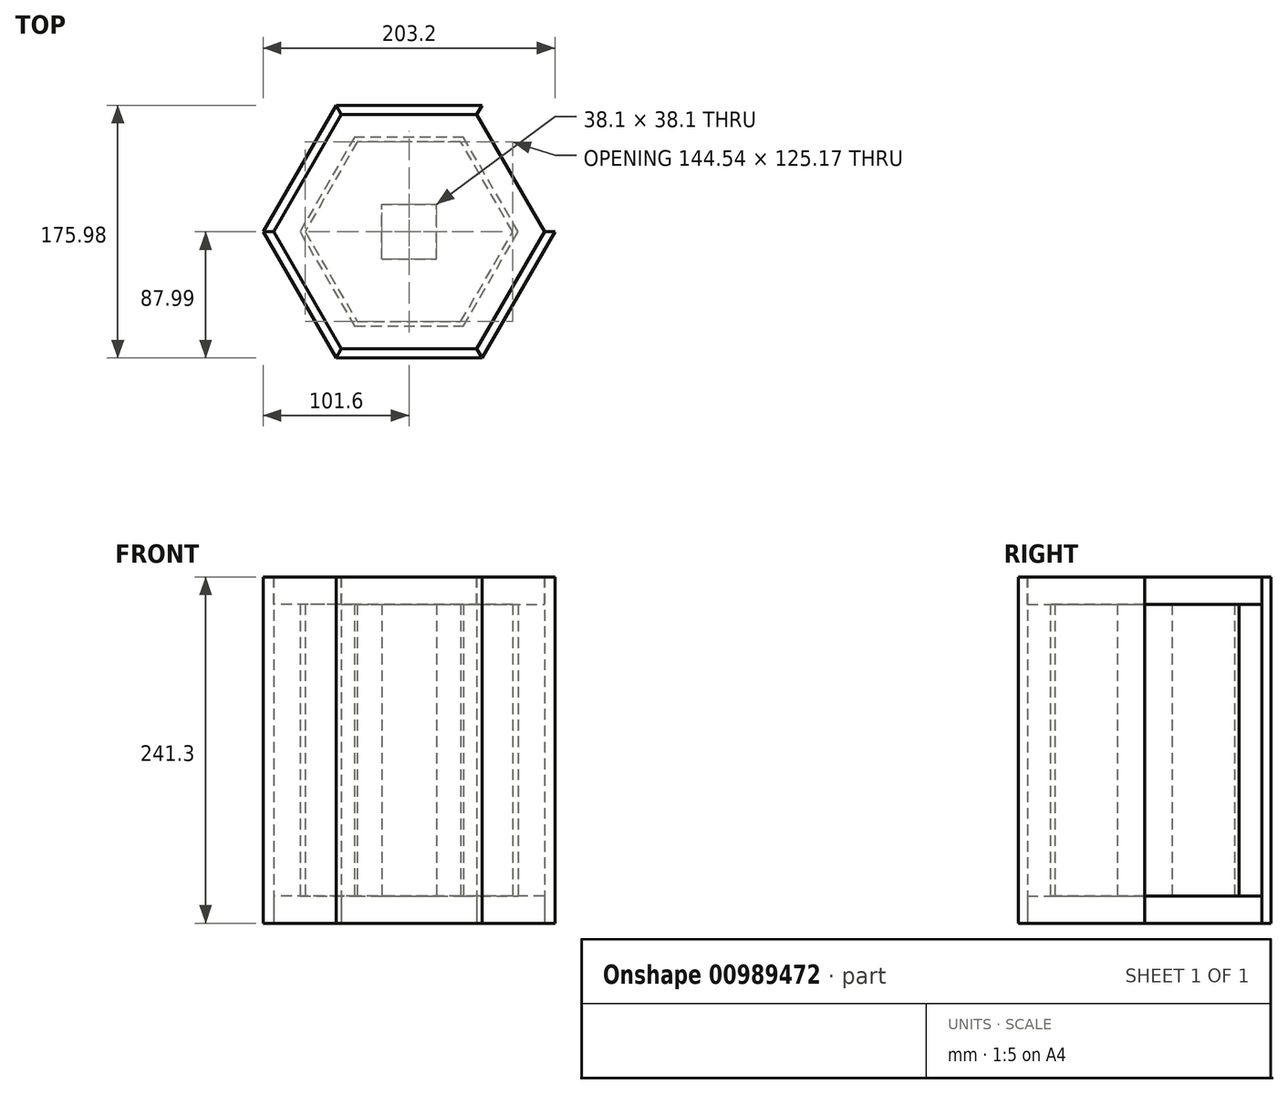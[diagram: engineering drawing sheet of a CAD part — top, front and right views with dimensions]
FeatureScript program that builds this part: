
annotation { "Feature Type Name" : "Feature", "Feature Type Description" : "" }
export const myFeature = defineFeature(function(context is Context, id is Id, definition is map)
    precondition{}
    {
        {
            var Q0;
            Q0=qCreatedBy(makeId("Top.planeOp"),FACE);
            var sketch = newSketch(context, id + "F0", { "sketchPlane" : qUnion([Q0])});
            skCircle(sketch, "E0.cCircle", {"center": v(0, 0) * mm, "radius": 87.99 * mm, "construction": true});
            skLineSegment(sketch, "E0.0", {"start": v(50.8, -87.99) * mm, "end": v(-50.8, -87.99) * mm});
            skLineSegment(sketch, "E0.1", {"start": v(-50.8, -87.99) * mm, "end": v(-101.6, 0) * mm});
            skLineSegment(sketch, "E0.2", {"start": v(-101.6, 0) * mm, "end": v(-50.8, 87.99) * mm});
            skLineSegment(sketch, "E0.3", {"start": v(-50.8, 87.99) * mm, "end": v(50.8, 87.99) * mm});
            skLineSegment(sketch, "E0.4", {"start": v(50.8, 87.99) * mm, "end": v(101.6, 0) * mm});
            skLineSegment(sketch, "E0.5", {"start": v(101.6, 0) * mm, "end": v(50.8, -87.99) * mm});
            skPoint(sketch, "E0.0.midPoint", {"position": v(0, -87.99) * mm});
            skLineSegment(sketch, "E1.0", {"start": v(-47.13, -81.64) * mm, "end": v(-94.26, 0) * mm});
            skLineSegment(sketch, "E1.1", {"start": v(-47.13, 81.64) * mm, "end": v(47.13, 81.64) * mm});
            skLineSegment(sketch, "E1.2", {"start": v(47.13, 81.64) * mm, "end": v(94.26, 0) * mm});
            skLineSegment(sketch, "E1.3", {"start": v(-94.26, 0) * mm, "end": v(-47.13, 81.64) * mm});
            skLineSegment(sketch, "E1.4", {"start": v(94.26, 0) * mm, "end": v(47.13, -81.64) * mm});
            skLineSegment(sketch, "E1.5", {"start": v(47.13, -81.64) * mm, "end": v(-47.13, -81.64) * mm});
            skLineSegment(sketch, "E2", {"start": v(-50.8, 87.99) * mm, "end": v(-47.13, 81.64) * mm});
            skLineSegment(sketch, "E3", {"start": v(47.13, 81.64) * mm, "end": v(50.8, 87.99) * mm});
            skLineSegment(sketch, "E4", {"start": v(101.6, 0) * mm, "end": v(94.26, 0) * mm});
            skLineSegment(sketch, "E5", {"start": v(47.13, -81.64) * mm, "end": v(50.8, -87.99) * mm});
            skLineSegment(sketch, "E6", {"start": v(-50.8, -87.99) * mm, "end": v(-47.13, -81.64) * mm});
            skLineSegment(sketch, "E7", {"start": v(-101.6, 0) * mm, "end": v(-94.26, 0) * mm});
            skSolve(sketch);
        }
        {
            var Q0;
            Q0=makeQuery(id+"F0.imprint","IMPRINT",FACE,{"disambiguationData":[TD([[makeQuery(id+"F0.imprint","IMPRINT",EDGE,{"derivedFrom":sQuery(id+"F0.wireOp",EDGE,"E1.0")}),-1.0]])]});
            extrude(context, id + "F1", {"entities" : qUnion([Q0]), "depth" : 19.05 * mm, "offsetDistance" : 25.4 * mm});
        }
        {
            var Q0;
            Q0=makeQuery(id+"F1.opExtrude","CAP_FACE",FACE,{"disambiguationData":[OSD([sQuery(id+"F0.wireOp",EDGE,"E1.0"),sQuery(id+"F0.wireOp",EDGE,"E1.1"),sQuery(id+"F0.wireOp",EDGE,"E1.2"),sQuery(id+"F0.wireOp",EDGE,"E1.3"),sQuery(id+"F0.wireOp",EDGE,"E1.4"),sQuery(id+"F0.wireOp",EDGE,"E1.5")])],"isStart":false});
            var sketch = newSketch(context, id + "F2", { "sketchPlane" : qUnion([Q0])});
            skLineSegment(sketch, "E8.bottom", {"start": v(-19.05, -19.05) * mm, "end": v(19.05, -19.05) * mm});
            skLineSegment(sketch, "E8.top", {"start": v(-19.05, 19.05) * mm, "end": v(19.05, 19.05) * mm});
            skLineSegment(sketch, "E8.left", {"start": v(-19.05, -19.05) * mm, "end": v(-19.05, 19.05) * mm});
            skLineSegment(sketch, "E8.right", {"start": v(19.05, -19.05) * mm, "end": v(19.05, 19.05) * mm});
            skSolve(sketch);
        }
        {
            var Q0;
            Q0=makeQuery(id+"F2.imprint","IMPRINT",FACE,{"disambiguationData":[TD([[makeQuery(id+"F2.imprint","IMPRINT",EDGE,{"derivedFrom":sQuery(id+"F2.wireOp",EDGE,"E8.bottom")}),1.0]])]});
            extrude(context, id + "F3", {"entities" : qUnion([Q0]), "depth" : 203.2 * mm, "offsetDistance" : 25.4 * mm});
        }
        {
            var Q0;
            Q0=makeQuery(id+"F1.opExtrude","CAP_FACE",FACE,{"disambiguationData":[OSD([sQuery(id+"F0.wireOp",EDGE,"E1.0"),sQuery(id+"F0.wireOp",EDGE,"E1.1"),sQuery(id+"F0.wireOp",EDGE,"E1.2"),sQuery(id+"F0.wireOp",EDGE,"E1.3"),sQuery(id+"F0.wireOp",EDGE,"E1.4"),sQuery(id+"F0.wireOp",EDGE,"E1.5")])],"isStart":false});
            cPlane(context, id + "F4", {"entities" : qUnion([Q0]), "cplaneType" : CPlaneType.OFFSET, "offset" : 101.6 * mm, "width" : 152.4 * mm, "height" : 152.4 * mm});
        }
        {
            var Q0;
            Q0=makeQuery(id+"F1.opExtrude","SWEPT_BODY",BODY,{"disambiguationData":[OSD([sQuery(id+"F0.wireOp",EDGE,"E1.0"),sQuery(id+"F0.wireOp",EDGE,"E1.1"),sQuery(id+"F0.wireOp",EDGE,"E1.2"),sQuery(id+"F0.wireOp",EDGE,"E1.3"),sQuery(id+"F0.wireOp",EDGE,"E1.4"),sQuery(id+"F0.wireOp",EDGE,"E1.5")])]});
            var Q1;
            Q1=qCreatedBy(id+"F4.planeOp",FACE);
            mirror(context, id + "F5", {"operationType" : NewBodyOperationType.ADD, "entities" : qUnion([Q0]), "mirrorPlane" : qUnion([Q1])});
        }
        {
            var Q0;
            Q0=makeQuery(id+"F0.imprint","IMPRINT",FACE,{"disambiguationData":[TD([[makeQuery(id+"F0.imprint","IMPRINT",EDGE,{"derivedFrom":sQuery(id+"F0.wireOp",EDGE,"E0.3")}),-1.0]])]});
            var Q1;
            Q1=makeQuery(id+"F5.opPattern","COPY",FACE,{"derivedFrom":makeQuery(id+"F1.opExtrude","CAP_FACE",FACE,{"disambiguationData":[OSD([sQuery(id+"F0.wireOp",EDGE,"E1.0"),sQuery(id+"F0.wireOp",EDGE,"E1.1"),sQuery(id+"F0.wireOp",EDGE,"E1.2"),sQuery(id+"F0.wireOp",EDGE,"E1.3"),sQuery(id+"F0.wireOp",EDGE,"E1.4"),sQuery(id+"F0.wireOp",EDGE,"E1.5")])],"isStart":true}),"instanceName":"1"});
            extrude(context, id + "F6", {"entities" : qUnion([Q0]), "endBound" : BoundingType.UP_TO_SURFACE, "depth" : 222.25 * mm, "endBoundEntityFace" : qUnion([Q1]), "offsetDistance" : 25.4 * mm});
        }
        {
            var Q0;
            Q0=makeQuery(id+"F0.imprint","IMPRINT",FACE,{"disambiguationData":[TD([[makeQuery(id+"F0.imprint","IMPRINT",EDGE,{"derivedFrom":sQuery(id+"F0.wireOp",EDGE,"E0.2")}),-1.0]])]});
            var Q1;
            Q1=makeQuery(id+"F5.opPattern","COPY",FACE,{"derivedFrom":makeQuery(id+"F1.opExtrude","CAP_FACE",FACE,{"disambiguationData":[OSD([sQuery(id+"F0.wireOp",EDGE,"E1.0"),sQuery(id+"F0.wireOp",EDGE,"E1.1"),sQuery(id+"F0.wireOp",EDGE,"E1.2"),sQuery(id+"F0.wireOp",EDGE,"E1.3"),sQuery(id+"F0.wireOp",EDGE,"E1.4"),sQuery(id+"F0.wireOp",EDGE,"E1.5")])],"isStart":true}),"instanceName":"1"});
            extrude(context, id + "F7", {"entities" : qUnion([Q0]), "endBound" : BoundingType.UP_TO_SURFACE, "depth" : 25.4 * mm, "endBoundEntityFace" : qUnion([Q1]), "offsetDistance" : 25.4 * mm});
        }
        {
            var Q0;
            Q0=makeQuery(id+"F0.imprint","IMPRINT",FACE,{"disambiguationData":[TD([[makeQuery(id+"F0.imprint","IMPRINT",EDGE,{"derivedFrom":sQuery(id+"F0.wireOp",EDGE,"E0.1")}),-1.0]])]});
            var Q1;
            Q1=makeQuery(id+"F5.opPattern","COPY",FACE,{"derivedFrom":makeQuery(id+"F1.opExtrude","CAP_FACE",FACE,{"disambiguationData":[OSD([sQuery(id+"F0.wireOp",EDGE,"E1.0"),sQuery(id+"F0.wireOp",EDGE,"E1.1"),sQuery(id+"F0.wireOp",EDGE,"E1.2"),sQuery(id+"F0.wireOp",EDGE,"E1.3"),sQuery(id+"F0.wireOp",EDGE,"E1.4"),sQuery(id+"F0.wireOp",EDGE,"E1.5")])],"isStart":true}),"instanceName":"1"});
            extrude(context, id + "F8", {"entities" : qUnion([Q0]), "endBound" : BoundingType.UP_TO_SURFACE, "depth" : 25.4 * mm, "endBoundEntityFace" : qUnion([Q1]), "offsetDistance" : 25.4 * mm});
        }
        {
            var Q0;
            Q0=makeQuery(id+"F0.imprint","IMPRINT",FACE,{"disambiguationData":[TD([[makeQuery(id+"F0.imprint","IMPRINT",EDGE,{"derivedFrom":sQuery(id+"F0.wireOp",EDGE,"E0.0")}),-1.0]])]});
            var Q1;
            Q1=makeQuery(id+"F5.opPattern","COPY",FACE,{"derivedFrom":makeQuery(id+"F1.opExtrude","CAP_FACE",FACE,{"disambiguationData":[OSD([sQuery(id+"F0.wireOp",EDGE,"E1.0"),sQuery(id+"F0.wireOp",EDGE,"E1.1"),sQuery(id+"F0.wireOp",EDGE,"E1.2"),sQuery(id+"F0.wireOp",EDGE,"E1.3"),sQuery(id+"F0.wireOp",EDGE,"E1.4"),sQuery(id+"F0.wireOp",EDGE,"E1.5")])],"isStart":true}),"instanceName":"1"});
            extrude(context, id + "F9", {"entities" : qUnion([Q0]), "endBound" : BoundingType.UP_TO_SURFACE, "depth" : 25.4 * mm, "endBoundEntityFace" : qUnion([Q1]), "offsetDistance" : 25.4 * mm});
        }
        {
            var Q0;
            Q0=makeQuery(id+"F0.imprint","IMPRINT",FACE,{"disambiguationData":[TD([[makeQuery(id+"F0.imprint","IMPRINT",EDGE,{"derivedFrom":sQuery(id+"F0.wireOp",EDGE,"E0.5")}),-1.0]])]});
            var Q1;
            Q1=makeQuery(id+"F5.opPattern","COPY",FACE,{"derivedFrom":makeQuery(id+"F1.opExtrude","CAP_FACE",FACE,{"disambiguationData":[OSD([sQuery(id+"F0.wireOp",EDGE,"E1.0"),sQuery(id+"F0.wireOp",EDGE,"E1.1"),sQuery(id+"F0.wireOp",EDGE,"E1.2"),sQuery(id+"F0.wireOp",EDGE,"E1.3"),sQuery(id+"F0.wireOp",EDGE,"E1.4"),sQuery(id+"F0.wireOp",EDGE,"E1.5")])],"isStart":true}),"instanceName":"1"});
            extrude(context, id + "F10", {"entities" : qUnion([Q0]), "endBound" : BoundingType.UP_TO_SURFACE, "depth" : 25.4 * mm, "endBoundEntityFace" : qUnion([Q1]), "offsetDistance" : 25.4 * mm});
        }
        {
            var Q0;
            Q0=makeQuery(id+"F1.opExtrude","CAP_FACE",FACE,{"disambiguationData":[OSD([sQuery(id+"F0.wireOp",EDGE,"E1.0"),sQuery(id+"F0.wireOp",EDGE,"E1.1"),sQuery(id+"F0.wireOp",EDGE,"E1.2"),sQuery(id+"F0.wireOp",EDGE,"E1.3"),sQuery(id+"F0.wireOp",EDGE,"E1.4"),sQuery(id+"F0.wireOp",EDGE,"E1.5")])],"isStart":false});
            var sketch = newSketch(context, id + "F11", { "sketchPlane" : qUnion([Q0])});
            skLineSegment(sketch, "E9.0", {"start": v(-36.13, -62.59) * mm, "end": v(-72.27, 0) * mm});
            skLineSegment(sketch, "E9.1", {"start": v(-36.13, 62.59) * mm, "end": v(36.13, 62.59) * mm});
            skLineSegment(sketch, "E9.2", {"start": v(36.13, 62.59) * mm, "end": v(72.27, 0) * mm});
            skLineSegment(sketch, "E9.3", {"start": v(-72.27, 0) * mm, "end": v(-36.13, 62.59) * mm});
            skLineSegment(sketch, "E9.4", {"start": v(72.27, 0) * mm, "end": v(36.13, -62.59) * mm});
            skLineSegment(sketch, "E9.5", {"start": v(36.13, -62.59) * mm, "end": v(-36.13, -62.59) * mm});
            skLineSegment(sketch, "E10.0", {"start": v(-37.97, -65.76) * mm, "end": v(-75.93, 0) * mm});
            skLineSegment(sketch, "E10.1", {"start": v(-37.97, 65.76) * mm, "end": v(37.97, 65.76) * mm});
            skLineSegment(sketch, "E10.2", {"start": v(37.97, 65.76) * mm, "end": v(75.93, 0) * mm});
            skLineSegment(sketch, "E10.3", {"start": v(-75.93, 0) * mm, "end": v(-37.97, 65.76) * mm});
            skLineSegment(sketch, "E10.4", {"start": v(75.93, 0) * mm, "end": v(37.97, -65.76) * mm});
            skLineSegment(sketch, "E10.5", {"start": v(37.97, -65.76) * mm, "end": v(-37.97, -65.76) * mm});
            skSolve(sketch);
        }
        {
            var Q0;
            Q0=makeQuery(id+"F11.imprint","IMPRINT",FACE,{"disambiguationData":[TD([[makeQuery(id+"F11.imprint","IMPRINT",EDGE,{"derivedFrom":sQuery(id+"F11.wireOp",EDGE,"E9.0")}),1.0]])]});
            var Q1;
            Q1=makeQuery(id+"F5.opPattern","COPY",FACE,{"derivedFrom":makeQuery(id+"F1.opExtrude","CAP_FACE",FACE,{"disambiguationData":[OSD([sQuery(id+"F0.wireOp",EDGE,"E1.0"),sQuery(id+"F0.wireOp",EDGE,"E1.1"),sQuery(id+"F0.wireOp",EDGE,"E1.2"),sQuery(id+"F0.wireOp",EDGE,"E1.3"),sQuery(id+"F0.wireOp",EDGE,"E1.4"),sQuery(id+"F0.wireOp",EDGE,"E1.5")])],"isStart":false}),"instanceName":"1"});
            extrude(context, id + "F12", {"entities" : qUnion([Q0]), "endBound" : BoundingType.UP_TO_SURFACE, "depth" : 25.4 * mm, "endBoundEntityFace" : qUnion([Q1]), "offsetDistance" : 25.4 * mm});
        }
    });
